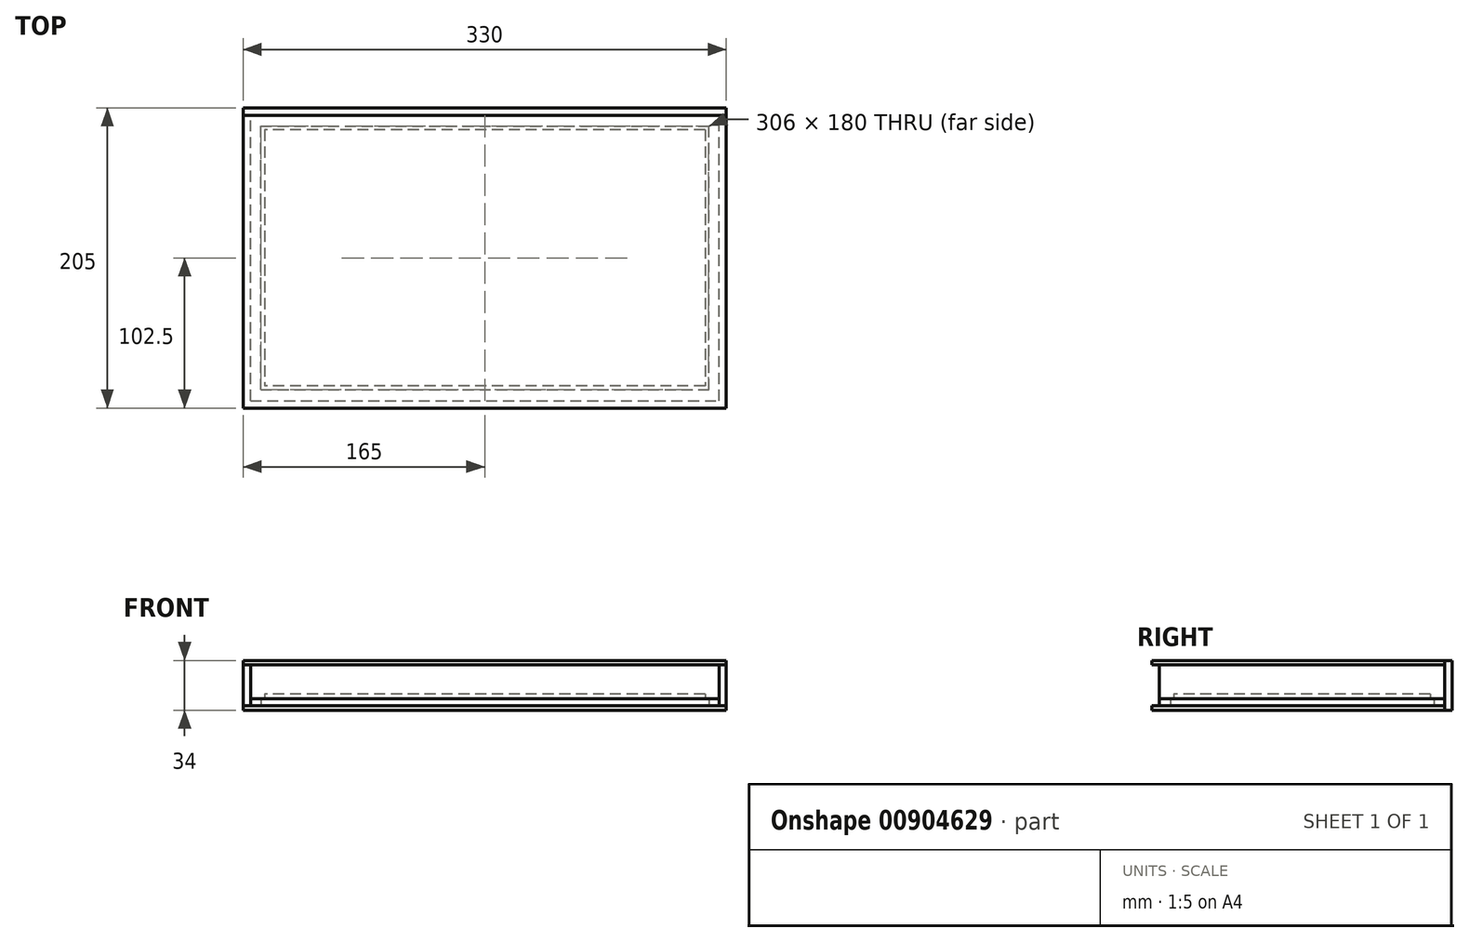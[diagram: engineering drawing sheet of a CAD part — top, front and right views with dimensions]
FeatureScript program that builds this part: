
annotation { "Feature Type Name" : "Feature", "Feature Type Description" : "" }
export const myFeature = defineFeature(function(context is Context, id is Id, definition is map)
    precondition{}
    {
        {
            var Q0;
            Q0=qCreatedBy(makeId("Top.planeOp"),FACE);
            var sketch = newSketch(context, id + "F0", { "sketchPlane" : qUnion([Q0])});
            skLineSegment(sketch, "E0.bottom", {"start": v(0, 0) * mm, "end": v(306, 0) * mm});
            skLineSegment(sketch, "E0.top", {"start": v(0, 180) * mm, "end": v(306, 180) * mm});
            skLineSegment(sketch, "E0.left", {"start": v(0, 0) * mm, "end": v(0, 180) * mm});
            skLineSegment(sketch, "E0.right", {"start": v(306, 0) * mm, "end": v(306, 180) * mm});
            skSolve(sketch);
        }
        {
            var Q0;
            Q0 = qSketchRegion(id + "F0", true);
            extrude(context, id + "F1", {"entities" : qUnion([Q0]), "depth" : 5 * mm, "offsetDistance" : 25 * mm});
        }
        {
            var Q0;
            Q0=qCreatedBy(makeId("Top.planeOp"),FACE);
            var sketch = newSketch(context, id + "F2", { "sketchPlane" : qUnion([Q0])});
            skLineSegment(sketch, "E1", {"start": v(0, 0) * mm, "end": v(153, 0) * mm, "construction": true});
            skLineSegment(sketch, "E2", {"start": v(153, 0) * mm, "end": v(153, 90) * mm, "construction": true});
            skLineSegment(sketch, "E3.bottom", {"start": v(-7, -7.5) * mm, "end": v(313, -7.5) * mm});
            skLineSegment(sketch, "E3.top", {"start": v(-7, 187.5) * mm, "end": v(313, 187.5) * mm});
            skLineSegment(sketch, "E3.left", {"start": v(-7, -7.5) * mm, "end": v(-7, 187.5) * mm});
            skLineSegment(sketch, "E3.right", {"start": v(313, -7.5) * mm, "end": v(313, 187.5) * mm});
            skPoint(sketch, "E3.middle", {"position": v(153, 90) * mm});
            skSolve(sketch);
        }
        {
            var Q0;
            Q0 = qSketchRegion(id + "F2", true);
            extrude(context, id + "F3", {"entities" : qUnion([Q0]), "depth" : 5 * mm, "offsetDistance" : 25 * mm});
        }
        {
            var Q0;
            Q0=makeQuery(id+"F1.opExtrude","SWEPT_BODY",BODY,{"disambiguationData":[OSD([sQuery(id+"F0.wireOp",EDGE,"E0.bottom"),sQuery(id+"F0.wireOp",EDGE,"E0.top"),sQuery(id+"F0.wireOp",EDGE,"E0.left"),sQuery(id+"F0.wireOp",EDGE,"E0.right")])]});
            var Q1;
            Q1=makeQuery(id+"F3.opExtrude","SWEPT_BODY",BODY,{"disambiguationData":[OSD([sQuery(id+"F2.wireOp",EDGE,"E3.bottom"),sQuery(id+"F2.wireOp",EDGE,"E3.top"),sQuery(id+"F2.wireOp",EDGE,"E3.left"),sQuery(id+"F2.wireOp",EDGE,"E3.right")])]});
            booleanBodies(context, id + "F4", {"operationType" : BooleanOperationType.SUBTRACTION, "tools" : qUnion([Q0]), "targets" : qUnion([Q1]), "keepTools" : true});
        }
        {
            var Q0;
            Q0=makeQuery(id+"F3.opExtrude","CAP_FACE",FACE,{"disambiguationData":[OSD([sQuery(id+"F2.wireOp",EDGE,"E3.bottom"),sQuery(id+"F2.wireOp",EDGE,"E3.top"),sQuery(id+"F2.wireOp",EDGE,"E3.left"),sQuery(id+"F2.wireOp",EDGE,"E3.right")])],"isStart":true});
            var sketch = newSketch(context, id + "F5", { "sketchPlane" : qUnion([Q0])});
            skLineSegment(sketch, "E4.bottom", {"start": v(313, -187.5) * mm, "end": v(-7, -187.5) * mm});
            skLineSegment(sketch, "E4.top", {"start": v(313, 7.5) * mm, "end": v(-7, 7.5) * mm});
            skLineSegment(sketch, "E4.left", {"start": v(313, -187.5) * mm, "end": v(313, 7.5) * mm});
            skLineSegment(sketch, "E4.right", {"start": v(-7, -187.5) * mm, "end": v(-7, 7.5) * mm});
            skLineSegment(sketch, "E5.bottom", {"start": v(-7, 7.5) * mm, "end": v(313, 7.5) * mm});
            skLineSegment(sketch, "E5.top", {"start": v(-7, 12.5) * mm, "end": v(313, 12.5) * mm});
            skLineSegment(sketch, "E5.left", {"start": v(-7, 7.5) * mm, "end": v(-7, 12.5) * mm});
            skLineSegment(sketch, "E5.right", {"start": v(313, 7.5) * mm, "end": v(313, 12.5) * mm});
            skLineSegment(sketch, "E6.bottom", {"start": v(313, 12.5) * mm, "end": v(318, 12.5) * mm});
            skLineSegment(sketch, "E6.top", {"start": v(313, -187.5) * mm, "end": v(318, -187.5) * mm});
            skLineSegment(sketch, "E6.left", {"start": v(313, 12.5) * mm, "end": v(313, -187.5) * mm});
            skLineSegment(sketch, "E6.right", {"start": v(318, 12.5) * mm, "end": v(318, -187.5) * mm});
            skLineSegment(sketch, "E7.bottom", {"start": v(-7, 12.5) * mm, "end": v(-12, 12.5) * mm});
            skLineSegment(sketch, "E7.top", {"start": v(-7, -187.5) * mm, "end": v(-12, -187.5) * mm});
            skLineSegment(sketch, "E7.left", {"start": v(-7, 12.5) * mm, "end": v(-7, -187.5) * mm});
            skLineSegment(sketch, "E7.right", {"start": v(-12, 12.5) * mm, "end": v(-12, -187.5) * mm});
            skSolve(sketch);
        }
        {
            var Q0;
            Q0 = qSketchRegion(id + "F5", true);
            extrude(context, id + "F6", {"entities" : qUnion([Q0]), "depth" : 3 * mm, "offsetDistance" : 25 * mm});
        }
        {
            var Q0;
            Q0=makeQuery(id+"F3.opExtrude","CAP_FACE",FACE,{"disambiguationData":[OSD([sQuery(id+"F2.wireOp",EDGE,"E3.bottom"),sQuery(id+"F2.wireOp",EDGE,"E3.top"),sQuery(id+"F2.wireOp",EDGE,"E3.left"),sQuery(id+"F2.wireOp",EDGE,"E3.right")])],"isStart":false});
            var sketch = newSketch(context, id + "F7", { "sketchPlane" : qUnion([Q0])});
            skLineSegment(sketch, "E8.bottom", {"start": v(-7, -7.5) * mm, "end": v(313, -7.5) * mm});
            skLineSegment(sketch, "E8.top", {"start": v(-7, 187.5) * mm, "end": v(313, 187.5) * mm});
            skLineSegment(sketch, "E8.left", {"start": v(-7, -7.5) * mm, "end": v(-7, 187.5) * mm});
            skLineSegment(sketch, "E8.right", {"start": v(313, -7.5) * mm, "end": v(313, 187.5) * mm});
            skLineSegment(sketch, "E9", {"start": v(0, 0) * mm, "end": v(2.5, 0) * mm, "construction": true});
            skLineSegment(sketch, "E10", {"start": v(2.5, 0) * mm, "end": v(2.5, 2.5) * mm, "construction": true});
            skLineSegment(sketch, "E11", {"start": v(306, 180) * mm, "end": v(303.5, 180) * mm, "construction": true});
            skLineSegment(sketch, "E12", {"start": v(303.5, 180) * mm, "end": v(303.5, 177.5) * mm, "construction": true});
            skLineSegment(sketch, "E13.bottom", {"start": v(303.5, 177.5) * mm, "end": v(2.5, 177.5) * mm});
            skLineSegment(sketch, "E13.top", {"start": v(303.5, 2.5) * mm, "end": v(2.5, 2.5) * mm});
            skLineSegment(sketch, "E13.left", {"start": v(303.5, 177.5) * mm, "end": v(303.5, 2.5) * mm});
            skLineSegment(sketch, "E13.right", {"start": v(2.5, 177.5) * mm, "end": v(2.5, 2.5) * mm});
            skSolve(sketch);
        }
        {
            var Q0;
            Q0 = qSketchRegion(id + "F7", true);
            extrude(context, id + "F8", {"entities" : qUnion([Q0]), "depth" : 3 * mm, "offsetDistance" : 25 * mm});
        }
        {
            var Q0;
            Q0=makeQuery(id+"F8.opExtrude","CAP_FACE",FACE,{"disambiguationData":[OSD([sQuery(id+"F7.wireOp",EDGE,"E8.bottom"),sQuery(id+"F7.wireOp",EDGE,"E8.top"),sQuery(id+"F7.wireOp",EDGE,"E8.left"),sQuery(id+"F7.wireOp",EDGE,"E8.right"),sQuery(id+"F7.wireOp",EDGE,"E13.bottom"),sQuery(id+"F7.wireOp",EDGE,"E13.top"),sQuery(id+"F7.wireOp",EDGE,"E13.left"),sQuery(id+"F7.wireOp",EDGE,"E13.right")])],"isStart":false});
            var sketch = newSketch(context, id + "F9", { "sketchPlane" : qUnion([Q0])});
            skLineSegment(sketch, "E14.bottom", {"start": v(313, 187.5) * mm, "end": v(-7, 187.5) * mm});
            skLineSegment(sketch, "E14.top", {"start": v(313, -7.5) * mm, "end": v(-7, -7.5) * mm});
            skLineSegment(sketch, "E14.left", {"start": v(313, 187.5) * mm, "end": v(313, -7.5) * mm});
            skLineSegment(sketch, "E14.right", {"start": v(-7, 187.5) * mm, "end": v(-7, -7.5) * mm});
            skSolve(sketch);
        }
        {
            var Q0;
            Q0 = qSketchRegion(id + "F9", true);
            extrude(context, id + "F10", {"entities" : qUnion([Q0]), "operationType" : NewBodyOperationType.ADD, "depth" : 20 * mm, "offsetDistance" : 25 * mm});
        }
        {
            var Q0;
            Q0=makeQuery(id+"F10.opExtrude","CAP_FACE",FACE,{"disambiguationData":[OSD([sQuery(id+"F9.wireOp",EDGE,"E14.bottom"),sQuery(id+"F9.wireOp",EDGE,"E14.top"),sQuery(id+"F9.wireOp",EDGE,"E14.left"),sQuery(id+"F9.wireOp",EDGE,"E14.right")])],"isStart":false});
            var sketch = newSketch(context, id + "F11", { "sketchPlane" : qUnion([Q0])});
            skLineSegment(sketch, "E15.bottom", {"start": v(313, -7.5) * mm, "end": v(-7, -7.5) * mm});
            skLineSegment(sketch, "E15.top", {"start": v(313, 187.5) * mm, "end": v(-7, 187.5) * mm});
            skLineSegment(sketch, "E15.left", {"start": v(313, -7.5) * mm, "end": v(313, 187.5) * mm});
            skLineSegment(sketch, "E15.right", {"start": v(-7, -7.5) * mm, "end": v(-7, 187.5) * mm});
            skLineSegment(sketch, "E16.top", {"start": v(313, -12.5) * mm, "end": v(-7, -12.5) * mm});
            skLineSegment(sketch, "E16.left", {"start": v(313, -7.5) * mm, "end": v(313, -12.5) * mm});
            skLineSegment(sketch, "E16.right", {"start": v(-7, -7.5) * mm, "end": v(-7, -12.5) * mm});
            skLineSegment(sketch, "E17.bottom", {"start": v(313, 187.5) * mm, "end": v(318, 187.5) * mm});
            skLineSegment(sketch, "E17.top", {"start": v(313, -12.5) * mm, "end": v(318, -12.5) * mm});
            skLineSegment(sketch, "E17.left", {"start": v(313, 187.5) * mm, "end": v(313, -12.5) * mm});
            skLineSegment(sketch, "E17.right", {"start": v(318, 187.5) * mm, "end": v(318, -12.5) * mm});
            skLineSegment(sketch, "E18.bottom", {"start": v(-7, -12.5) * mm, "end": v(-12, -12.5) * mm});
            skLineSegment(sketch, "E18.top", {"start": v(-7, 187.5) * mm, "end": v(-12, 187.5) * mm});
            skLineSegment(sketch, "E18.left", {"start": v(-7, -12.5) * mm, "end": v(-7, 187.5) * mm});
            skLineSegment(sketch, "E18.right", {"start": v(-12, -12.5) * mm, "end": v(-12, 187.5) * mm});
            skSolve(sketch);
        }
        {
            var Q0;
            Q0 = qSketchRegion(id + "F11", true);
            extrude(context, id + "F12", {"entities" : qUnion([Q0]), "depth" : 3 * mm, "offsetDistance" : 25 * mm});
        }
        {
            var Q0;
            Q0=makeQuery(id+"F6.opExtrude","SWEPT_FACE",FACE,{"disambiguationData":[OSD([sQuery(id+"F5.wireOp",EDGE,"E4.bottom"),sQuery(id+"F5.wireOp",EDGE,"E6.top"),sQuery(id+"F5.wireOp",EDGE,"E7.top")])]});
            var sketch = newSketch(context, id + "F13", { "sketchPlane" : qUnion([Q0])});
            skLineSegment(sketch, "E19.bottom", {"start": v(12, -3) * mm, "end": v(-318, -3) * mm});
            skLineSegment(sketch, "E19.top", {"start": v(12, 31) * mm, "end": v(-318, 31) * mm});
            skLineSegment(sketch, "E19.left", {"start": v(12, -3) * mm, "end": v(12, 31) * mm});
            skLineSegment(sketch, "E19.right", {"start": v(-318, -3) * mm, "end": v(-318, 31) * mm});
            skSolve(sketch);
        }
        {
            var Q0;
            Q0 = qSketchRegion(id + "F13", true);
            extrude(context, id + "F14", {"entities" : qUnion([Q0]), "depth" : 5 * mm, "offsetDistance" : 25 * mm});
        }
    });
